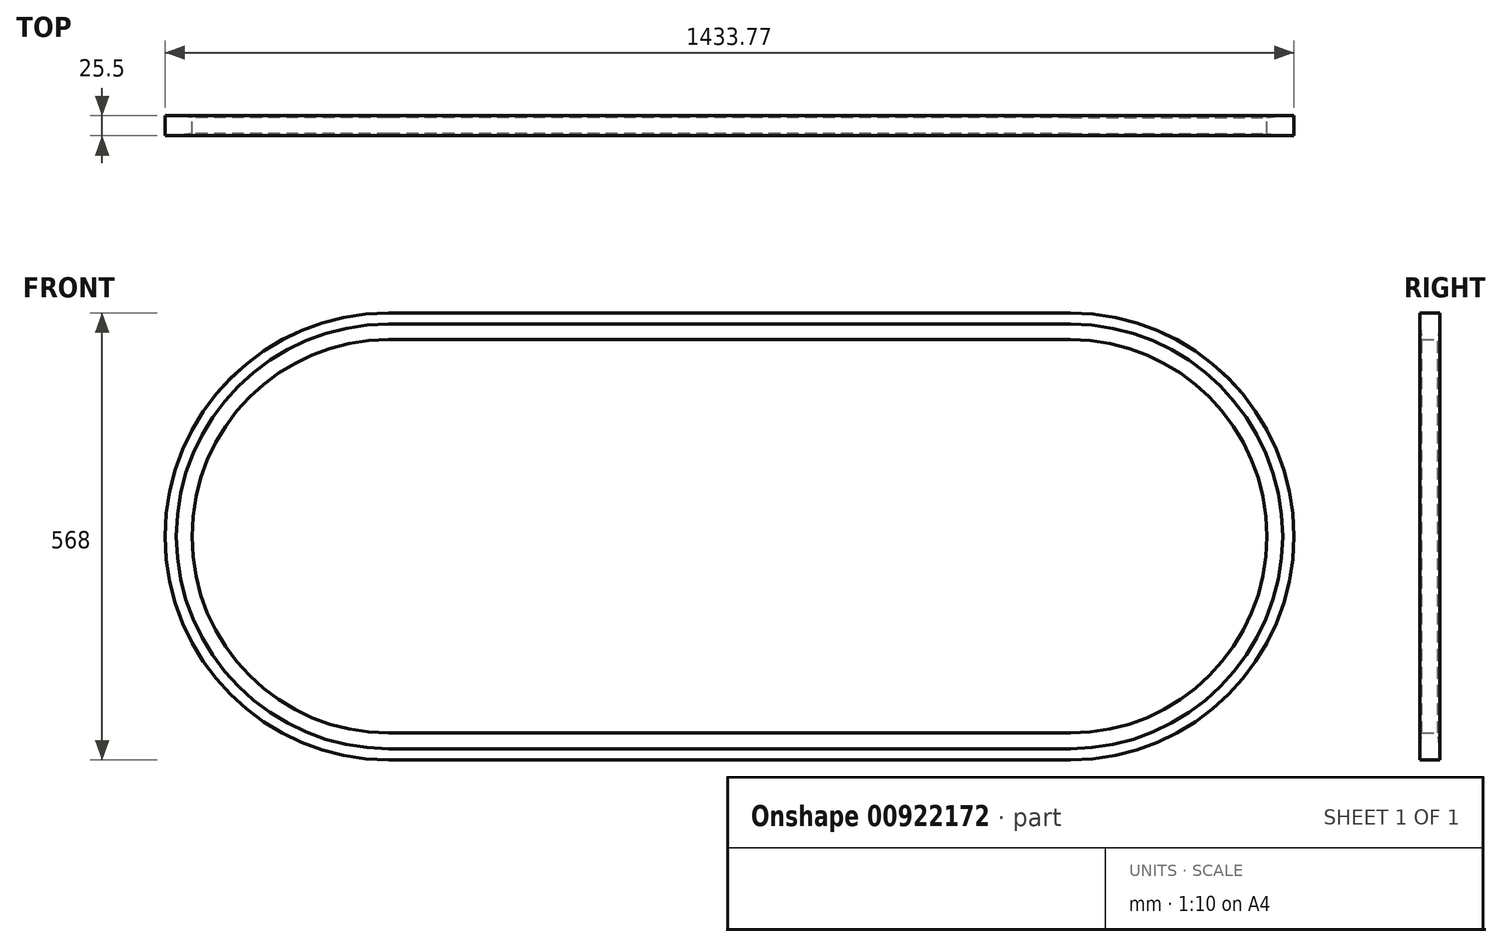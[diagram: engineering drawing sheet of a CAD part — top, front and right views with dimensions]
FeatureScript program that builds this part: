
annotation { "Feature Type Name" : "Feature", "Feature Type Description" : "" }
export const myFeature = defineFeature(function(context is Context, id is Id, definition is map)
    precondition{}
    {
        {
            var Q0;
            Q0=qCreatedBy(makeId("Right.planeOp"),FACE);
            var sketch = newSketch(context, id + "F0", { "sketchPlane" : qUnion([Q0])});
            skLineSegment(sketch, "E0.MirrorCS", {"start": v(12.73, 269.82) * mm, "end": v(10.01, 250) * mm});
            skLineSegment(sketch, "E1", {"start": v(12.73, 269.82) * mm, "end": v(12.73, 284) * mm});
            skLineSegment(sketch, "E2.MirrorCS", {"start": v(-12.74, 269.8) * mm, "end": v(-12.77, 283.97) * mm});
            skLineSegment(sketch, "E3.MirrorCS", {"start": v(-12.74, 269.8) * mm, "end": v(-9.99, 250) * mm});
            skLineSegment(sketch, "E4", {"start": v(-9.99, 250) * mm, "end": v(10.01, 250) * mm});
            skLineSegment(sketch, "E5", {"start": v(-12.77, 283.97) * mm, "end": v(12.73, 284) * mm});
            skSolve(sketch);
        }
        {
            var Q0;
            Q0=qCreatedBy(makeId("Front.planeOp"),FACE);
            var sketch = newSketch(context, id + "F1", { "sketchPlane" : qUnion([Q0])});
            skLineSegment(sketch, "E6", {"start": v(0, 267) * mm, "end": v(865.77, 267) * mm});
            skArc(sketch, "E7", {"start": v(0, 267) * mm, "mid": v(-267, 0) * mm, "end": v(0, -267) * mm});
            skArc(sketch, "E8", {"start": v(865.77, -267) * mm, "mid": v(1132.77, 0) * mm, "end": v(865.77, 267) * mm});
            skLineSegment(sketch, "E9", {"start": v(0, -267) * mm, "end": v(865.77, -267) * mm});
            skSolve(sketch);
        }
        {
            var Q0;
            Q0 = qSketchRegion(id + "F0", true);
            var Q1;
            Q1 = qConstructionFilter(qBodyType(qCreatedBy(id + "F1" ,EDGE), BodyType.WIRE), ConstructionObject.NO);
            sweep(context, id + "F2", {"profiles" : qUnion([Q0]), "path" : qUnion([Q1])});
        }
    });
